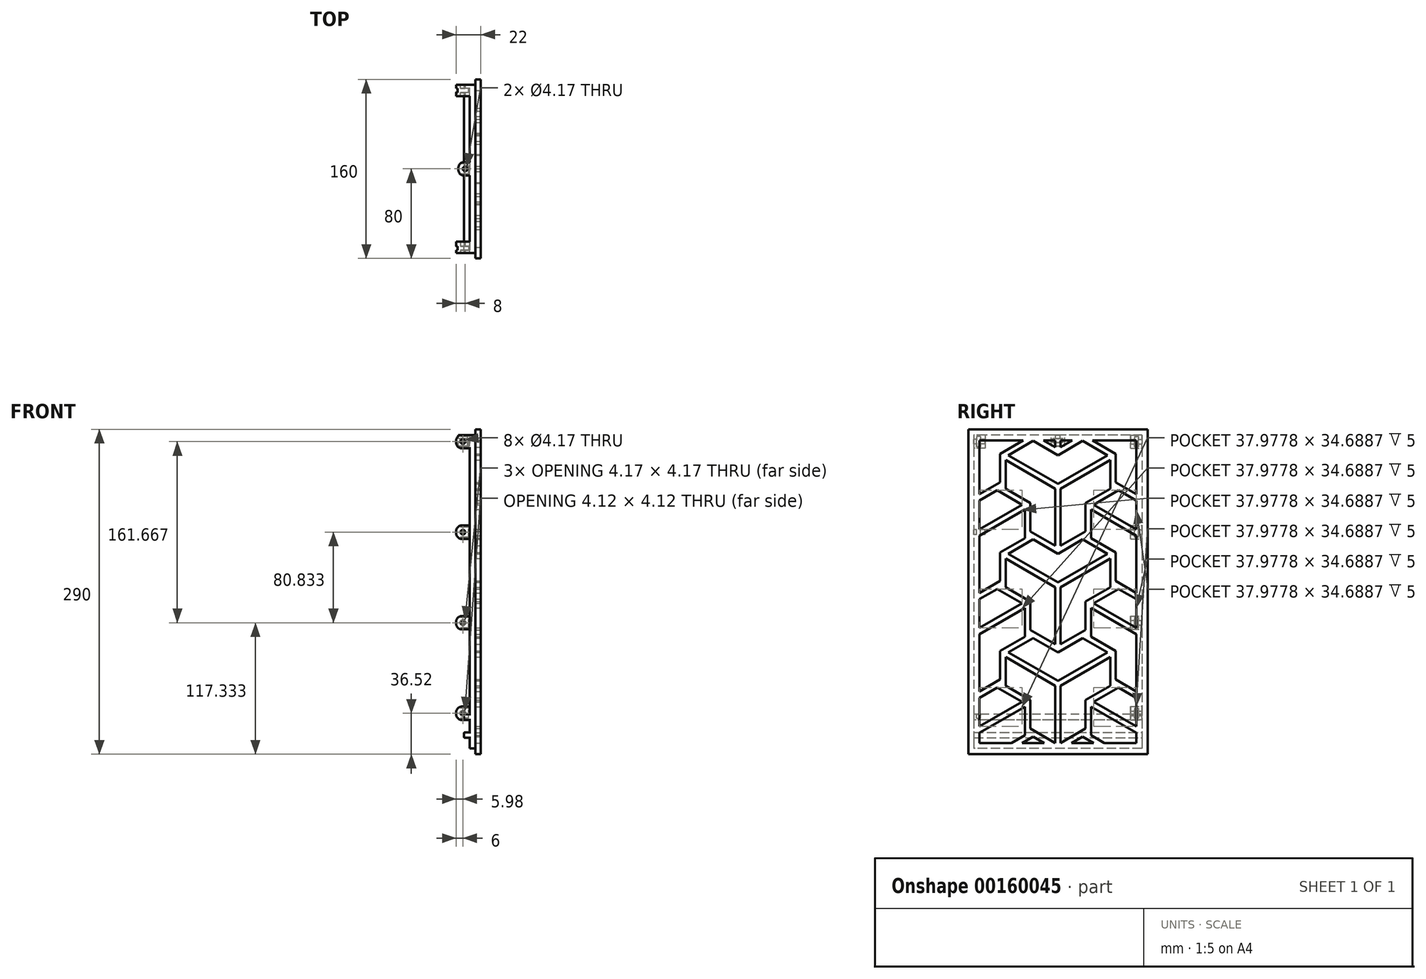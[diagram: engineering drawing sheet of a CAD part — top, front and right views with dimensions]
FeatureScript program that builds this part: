
annotation { "Feature Type Name" : "Feature", "Feature Type Description" : "" }
export const myFeature = defineFeature(function(context is Context, id is Id, definition is map)
    precondition{}
    {
        {
            var Q0;
            Q0=qCreatedBy(makeId("Top.planeOp"),FACE);
            var sketch = newSketch(context, id + "F0", { "sketchPlane" : qUnion([Q0])});
            skLineSegment(sketch, "E0.bottom", {"start": v(-72.5, -75) * mm, "end": v(72.5, -75) * mm});
            skLineSegment(sketch, "E0.top", {"start": v(-72.5, 75) * mm, "end": v(72.5, 75) * mm});
            skLineSegment(sketch, "E0.left", {"start": v(-72.5, -75) * mm, "end": v(-72.5, 75) * mm});
            skLineSegment(sketch, "E0.right", {"start": v(72.5, -75) * mm, "end": v(72.5, 75) * mm});
            skPoint(sketch, "E0.middle", {"position": v(0, 0) * mm});
            skLineSegment(sketch, "E1.bottom", {"start": v(-82.5, -85) * mm, "end": v(82.5, -85) * mm});
            skLineSegment(sketch, "E1.top", {"start": v(-82.5, 85) * mm, "end": v(82.5, 85) * mm});
            skLineSegment(sketch, "E1.left", {"start": v(-82.5, -85) * mm, "end": v(-82.5, 85) * mm});
            skLineSegment(sketch, "E1.right", {"start": v(82.5, -85) * mm, "end": v(82.5, 85) * mm});
            skLineSegment(sketch, "E2", {"start": v(82.5, -80) * mm, "end": v(77.5, -80) * mm});
            skLineSegment(sketch, "E3", {"start": v(77.5, -80) * mm, "end": v(77.5, -75) * mm});
            skLineSegment(sketch, "E4", {"start": v(77.5, -75) * mm, "end": v(72.5, -75) * mm});
            skLineSegment(sketch, "E5", {"start": v(0, -85) * mm, "end": v(0, 85) * mm, "construction": true});
            skLineSegment(sketch, "E6", {"start": v(-82.5, 0) * mm, "end": v(82.5, 0) * mm, "construction": true});
            skLineSegment(sketch, "E7.MirrorCS", {"start": v(-77.5, -75) * mm, "end": v(-72.5, -75) * mm});
            skLineSegment(sketch, "E8.MirrorCS", {"start": v(-77.5, -80) * mm, "end": v(-77.5, -75) * mm});
            skLineSegment(sketch, "E9.MirrorCS", {"start": v(-82.5, -80) * mm, "end": v(-77.5, -80) * mm});
            skLineSegment(sketch, "E10.MirrorCS", {"start": v(82.5, 80) * mm, "end": v(77.5, 80) * mm});
            skLineSegment(sketch, "E11.MirrorCS", {"start": v(77.5, 80) * mm, "end": v(77.5, 75) * mm});
            skLineSegment(sketch, "E12.MirrorCS", {"start": v(77.5, 75) * mm, "end": v(72.5, 75) * mm});
            skLineSegment(sketch, "E13.MirrorCS", {"start": v(-77.5, 75) * mm, "end": v(-72.5, 75) * mm});
            skLineSegment(sketch, "E14.MirrorCS", {"start": v(-77.5, 80) * mm, "end": v(-77.5, 75) * mm});
            skLineSegment(sketch, "E15.MirrorCS", {"start": v(-82.5, 80) * mm, "end": v(-77.5, 80) * mm});
            skSolve(sketch);
        }
        {
            var Q0;
            Q0=makeQuery(id+"F0.imprint","IMPRINT",FACE,{"disambiguationData":[TD([[makeQuery(id+"F0.imprint","IMPRINT",EDGE,{"derivedFrom":sQuery(id+"F0.wireOp",EDGE,"E0.right")}),-1.0]])]});
            extrude(context, id + "F1", {"entities" : qUnion([Q0]), "depth" : 290 * mm});
        }
        {
            var Q0;
            Q0=makeQuery(id+"F1.opExtrude","SWEPT_FACE",FACE,{"disambiguationData":[OSD([sQuery(id+"F0.wireOp",EDGE,"E4")])]});
            var sketch = newSketch(context, id + "F2", { "sketchPlane" : qUnion([Q0])});
            skLineSegment(sketch, "E16.bottom", {"start": v(77.5, 290) * mm, "end": v(72.5, 290) * mm});
            skLineSegment(sketch, "E16.top", {"start": v(77.5, 285) * mm, "end": v(72.5, 285) * mm});
            skLineSegment(sketch, "E16.left", {"start": v(77.5, 290) * mm, "end": v(77.5, 285) * mm});
            skLineSegment(sketch, "E16.right", {"start": v(72.5, 290) * mm, "end": v(72.5, 285) * mm});
            skLineSegment(sketch, "E17.bottom", {"start": v(77.5, 0) * mm, "end": v(72.5, 0) * mm});
            skLineSegment(sketch, "E17.top", {"start": v(77.5, 5) * mm, "end": v(72.5, 5) * mm});
            skLineSegment(sketch, "E17.left", {"start": v(77.5, 0) * mm, "end": v(77.5, 5) * mm});
            skLineSegment(sketch, "E17.right", {"start": v(72.5, 0) * mm, "end": v(72.5, 5) * mm});
            skSolve(sketch);
        }
        {
            var Q0;
            Q0 = qSketchRegion(id + "F2", true);
            extrude(context, id + "F3", {"entities" : qUnion([Q0]), "operationType" : NewBodyOperationType.REMOVE, "endBound" : BoundingType.THROUGH_ALL, "oppositeDirection" : true, "depth" : 25 * mm});
        }
        {
            var Q0;
            Q0=makeQuery(id+"F1.opExtrude","SWEPT_FACE",FACE,{"disambiguationData":[OSD([sQuery(id+"F0.wireOp",EDGE,"E0.right")])]});
            var sketch = newSketch(context, id + "F4", { "sketchPlane" : qUnion([Q0])});
            skLineSegment(sketch, "E18.bottom", {"start": v(-75, 35.5) * mm, "end": v(75, 35.5) * mm});
            skLineSegment(sketch, "E18.top", {"start": v(-75, 30.5) * mm, "end": v(75, 30.5) * mm});
            skLineSegment(sketch, "E18.left", {"start": v(-75, 35.5) * mm, "end": v(-75, 30.5) * mm});
            skLineSegment(sketch, "E18.right", {"start": v(75, 35.5) * mm, "end": v(75, 30.5) * mm});
            skLineSegment(sketch, "E19.bottom", {"start": v(75, 19.5) * mm, "end": v(-75, 19.5) * mm});
            skLineSegment(sketch, "E19.top", {"start": v(75, 14.5) * mm, "end": v(-75, 14.5) * mm});
            skLineSegment(sketch, "E19.left", {"start": v(75, 19.5) * mm, "end": v(75, 14.5) * mm});
            skLineSegment(sketch, "E19.right", {"start": v(-75, 19.5) * mm, "end": v(-75, 14.5) * mm});
            skSolve(sketch);
        }
        {
            var Q0;
            Q0=makeQuery(id+"F4.imprint","IMPRINT",FACE,{"disambiguationData":[TD([[makeQuery(id+"F4.imprint","IMPRINT",EDGE,{"derivedFrom":sQuery(id+"F4.wireOp",EDGE,"jm3xENIU-WNiL-2Yo7-S2n1-P718Q5YoGy5W.bottom")}),-1.0]])]});
            var Q1;
            Q1=makeQuery(id+"F4.imprint","IMPRINT",FACE,{"disambiguationData":[TD([[makeQuery(id+"F4.imprint","IMPRINT",EDGE,{"derivedFrom":sQuery(id+"F4.wireOp",EDGE,"tnRABQw2-jlkN-R6kw-IWLg-kbEZeZclKpCx.bottom")}),1.0]])]});
            var Q2;
            Q2=makeQuery(id+"F4.imprint","IMPRINT",FACE,{"disambiguationData":[TD([[makeQuery(id+"F4.imprint","IMPRINT",EDGE,{"derivedFrom":sQuery(id+"F4.wireOp",EDGE,"E18.bottom")}),-1.0]])]});
            var Q3;
            Q3=makeQuery(id+"F4.imprint","IMPRINT",FACE,{"disambiguationData":[TD([[makeQuery(id+"F4.imprint","IMPRINT",EDGE,{"derivedFrom":sQuery(id+"F4.wireOp",EDGE,"E19.bottom")}),1.0]])]});
            extrude(context, id + "F5", {"entities" : qUnion([Q0, Q1, Q2, Q3]), "operationType" : NewBodyOperationType.ADD, "depth" : 5 * mm});
        }
        {
            var Q0;
            Q0=makeQuery(id+"F1.opExtrude","SWEPT_FACE",FACE,{"disambiguationData":[OSD([sQuery(id+"F0.wireOp",EDGE,"E1.right")])]});
            var sketch = newSketch(context, id + "F6", { "sketchPlane" : qUnion([Q0])});
            skLineSegment(sketch, "E20.left", {"start": v(70, 10) * mm, "end": v(70, 280) * mm, "construction": true});
            skPoint(sketch, "E20.middle", {"position": v(0, 145) * mm});
            skPoint(sketch, "E20.middle.positionSnap0", {"position": v(-80, 145) * mm});
            skPoint(sketch, "E20.middle.positionSnap1", {"position": v(0, 290) * mm});
            skPoint(sketch, "E20.centerSnap0", {"position": v(-80, 145) * mm});
            skPoint(sketch, "E20.centerSnap1", {"position": v(0, 290) * mm});
            skLineSegment(sketch, "E21", {"start": v(-70, 280) * mm, "end": v(70, 280) * mm, "construction": true});
            skLineSegment(sketch, "E22", {"start": v(-70, 10) * mm, "end": v(70, 10) * mm, "construction": true});
            skLineSegment(sketch, "E23", {"start": v(-70, 280) * mm, "end": v(-70, 10) * mm, "construction": true});
            skLineSegment(sketch, "E24", {"start": v(2.5, 10) * mm, "end": v(2.5, 61.05) * mm});
            skLineSegment(sketch, "E25", {"start": v(2.5, 61.05) * mm, "end": v(46.7, 86.57) * mm});
            skLineSegment(sketch, "E26", {"start": v(46.7, 86.57) * mm, "end": v(46.7, 61.05) * mm});
            skLineSegment(sketch, "E27", {"start": v(2.5, 10) * mm, "end": v(24.6, 22.76) * mm});
            skLineSegment(sketch, "E28", {"start": v(24.6, 22.76) * mm, "end": v(24.6, 48.29) * mm});
            skLineSegment(sketch, "E29", {"start": v(24.6, 48.29) * mm, "end": v(46.7, 61.05) * mm});
            skLineSegment(sketch, "E30.1.0", {"start": v(0, 65.38) * mm, "end": v(-44.2, 90.9) * mm});
            skLineSegment(sketch, "E30.1.1", {"start": v(-44.2, 90.9) * mm, "end": v(-22.1, 103.67) * mm});
            skLineSegment(sketch, "E30.1.2", {"start": v(0, 90.9) * mm, "end": v(-22.1, 103.67) * mm});
            skLineSegment(sketch, "E30.1.3", {"start": v(22.1, 103.67) * mm, "end": v(0, 90.9) * mm});
            skLineSegment(sketch, "E30.1.4", {"start": v(44.2, 90.9) * mm, "end": v(22.1, 103.67) * mm});
            skLineSegment(sketch, "E30.1.5", {"start": v(44.2, 90.9) * mm, "end": v(0, 65.38) * mm});
            skLineSegment(sketch, "E30.2.0", {"start": v(-2.5, 61.05) * mm, "end": v(-2.5, 10) * mm});
            skLineSegment(sketch, "E30.2.1", {"start": v(-2.5, 10) * mm, "end": v(-24.6, 22.76) * mm});
            skLineSegment(sketch, "E30.2.2", {"start": v(-24.6, 48.29) * mm, "end": v(-24.6, 22.76) * mm});
            skLineSegment(sketch, "E30.2.3", {"start": v(-46.7, 61.05) * mm, "end": v(-24.6, 48.29) * mm});
            skLineSegment(sketch, "E30.2.4", {"start": v(-46.7, 86.57) * mm, "end": v(-46.7, 61.05) * mm});
            skLineSegment(sketch, "E30.2.5", {"start": v(-46.7, 86.57) * mm, "end": v(-2.5, 61.05) * mm});
            skPoint(sketch, "E30.center", {"position": v(0, 62.5) * mm});
            skLineSegment(sketch, "E31.0.1.0", {"start": v(2.5, 98) * mm, "end": v(2.5, 149.05) * mm});
            skLineSegment(sketch, "E31.0.1.1", {"start": v(2.5, 98) * mm, "end": v(24.6, 110.76) * mm});
            skLineSegment(sketch, "E31.0.1.2", {"start": v(24.6, 110.76) * mm, "end": v(24.6, 136.29) * mm});
            skLineSegment(sketch, "E31.0.1.3", {"start": v(24.6, 136.29) * mm, "end": v(46.7, 149.05) * mm});
            skLineSegment(sketch, "E31.0.1.4", {"start": v(46.7, 174.57) * mm, "end": v(46.7, 149.05) * mm});
            skLineSegment(sketch, "E31.0.1.5", {"start": v(2.5, 149.05) * mm, "end": v(46.7, 174.57) * mm});
            skLineSegment(sketch, "E31.0.1.6", {"start": v(44.2, 178.9) * mm, "end": v(0, 153.38) * mm});
            skLineSegment(sketch, "E31.0.1.7", {"start": v(44.2, 178.9) * mm, "end": v(22.1, 191.67) * mm});
            skLineSegment(sketch, "E31.0.1.8", {"start": v(22.1, 191.67) * mm, "end": v(0, 178.9) * mm});
            skLineSegment(sketch, "E31.0.2.0", {"start": v(2.5, 186) * mm, "end": v(2.5, 237.05) * mm});
            skLineSegment(sketch, "E31.0.2.1", {"start": v(2.5, 186) * mm, "end": v(24.6, 198.76) * mm});
            skLineSegment(sketch, "E31.0.2.2", {"start": v(24.6, 198.76) * mm, "end": v(24.6, 224.29) * mm});
            skLineSegment(sketch, "E31.0.2.3", {"start": v(24.6, 224.29) * mm, "end": v(46.7, 237.05) * mm});
            skLineSegment(sketch, "E31.0.2.4", {"start": v(46.7, 262.57) * mm, "end": v(46.7, 237.05) * mm});
            skLineSegment(sketch, "E31.0.2.5", {"start": v(2.5, 237.05) * mm, "end": v(46.7, 262.57) * mm});
            skLineSegment(sketch, "E31.0.2.6", {"start": v(44.2, 266.9) * mm, "end": v(0, 241.38) * mm});
            skLineSegment(sketch, "E31.0.2.7", {"start": v(44.2, 266.9) * mm, "end": v(22.1, 279.67) * mm});
            skLineSegment(sketch, "E31.0.2.8", {"start": v(22.1, 279.67) * mm, "end": v(0, 266.9) * mm});
            skLineSegment(sketch, "E31.0.3.0", {"start": v(2.5, 274) * mm, "end": v(2.5, 280) * mm});
            skLineSegment(sketch, "E31.0.3.1", {"start": v(2.5, 274) * mm, "end": v(12.9, 280) * mm});
            skLineSegment(sketch, "E32.0.1.5", {"start": v(29.52, 42.41) * mm, "end": v(70, 19.04) * mm});
            skLineSegment(sketch, "E32.0.1.6", {"start": v(29.52, 16.89) * mm, "end": v(41.45, 10) * mm});
            skLineSegment(sketch, "E32.0.1.9", {"start": v(29.52, 42.41) * mm, "end": v(29.52, 16.89) * mm});
            skLineSegment(sketch, "E32.0.1.15", {"start": v(70, 50.34) * mm, "end": v(54.13, 59.5) * mm});
            skLineSegment(sketch, "E32.0.1.16", {"start": v(32.02, 46.74) * mm, "end": v(54.13, 59.5) * mm});
            skLineSegment(sketch, "E32.0.1.17", {"start": v(70, 24.81) * mm, "end": v(32.02, 46.74) * mm});
            skLineSegment(sketch, "E33.0.1.4", {"start": v(70, 112.81) * mm, "end": v(32.02, 134.74) * mm});
            skLineSegment(sketch, "E33.0.1.5", {"start": v(29.52, 130.41) * mm, "end": v(70, 107.04) * mm});
            skLineSegment(sketch, "E33.0.1.7", {"start": v(29.52, 130.41) * mm, "end": v(29.52, 104.89) * mm});
            skLineSegment(sketch, "E33.0.1.9", {"start": v(51.63, 92.12) * mm, "end": v(51.63, 66.6) * mm});
            skLineSegment(sketch, "E33.0.1.10", {"start": v(70, 56) * mm, "end": v(51.63, 66.6) * mm});
            skLineSegment(sketch, "E33.0.1.12", {"start": v(29.52, 104.89) * mm, "end": v(51.63, 92.12) * mm});
            skLineSegment(sketch, "E33.0.1.13", {"start": v(32.02, 134.74) * mm, "end": v(54.13, 147.5) * mm});
            skLineSegment(sketch, "E33.0.1.14", {"start": v(70, 138.34) * mm, "end": v(54.13, 147.5) * mm});
            skLineSegment(sketch, "E33.0.2.4", {"start": v(70, 200.81) * mm, "end": v(32.02, 222.74) * mm});
            skLineSegment(sketch, "E33.0.2.5", {"start": v(29.52, 218.41) * mm, "end": v(70, 195.04) * mm});
            skLineSegment(sketch, "E33.0.2.7", {"start": v(29.52, 218.41) * mm, "end": v(29.52, 192.89) * mm});
            skLineSegment(sketch, "E33.0.2.9", {"start": v(51.63, 180.12) * mm, "end": v(51.63, 154.6) * mm});
            skLineSegment(sketch, "E33.0.2.10", {"start": v(70, 144) * mm, "end": v(51.63, 154.6) * mm});
            skLineSegment(sketch, "E33.0.2.12", {"start": v(29.52, 192.89) * mm, "end": v(51.63, 180.12) * mm});
            skLineSegment(sketch, "E33.0.2.13", {"start": v(32.02, 222.74) * mm, "end": v(54.13, 235.5) * mm});
            skLineSegment(sketch, "E33.0.2.14", {"start": v(70, 226.34) * mm, "end": v(54.13, 235.5) * mm});
            skLineSegment(sketch, "E33.0.3.9", {"start": v(51.63, 268.12) * mm, "end": v(51.63, 242.6) * mm});
            skLineSegment(sketch, "E33.0.3.10", {"start": v(70, 232) * mm, "end": v(51.63, 242.6) * mm});
            skLineSegment(sketch, "E33.0.3.12", {"start": v(31.06, 280) * mm, "end": v(51.63, 268.12) * mm});
            skLineSegment(sketch, "E34", {"start": v(0, 280) * mm, "end": v(0, 10) * mm, "construction": true});
            skLineSegment(sketch, "E35", {"start": v(41.45, 10) * mm, "end": v(70, 10) * mm});
            skLineSegment(sketch, "E36", {"start": v(70, 10) * mm, "end": v(70, 19.04) * mm});
            skLineSegment(sketch, "E37", {"start": v(70, 24.81) * mm, "end": v(70, 50.34) * mm});
            skLineSegment(sketch, "E38", {"start": v(70, 56) * mm, "end": v(70, 107.04) * mm});
            skLineSegment(sketch, "E39", {"start": v(70, 112.81) * mm, "end": v(70, 138.34) * mm});
            skLineSegment(sketch, "E40", {"start": v(70, 144) * mm, "end": v(70, 195.04) * mm});
            skLineSegment(sketch, "E41", {"start": v(70, 200.81) * mm, "end": v(70, 226.34) * mm});
            skLineSegment(sketch, "E42", {"start": v(70, 232) * mm, "end": v(70, 280) * mm});
            skLineSegment(sketch, "E43", {"start": v(12.9, 280) * mm, "end": v(2.5, 280) * mm});
            skLineSegment(sketch, "E44", {"start": v(70, 280) * mm, "end": v(31.06, 280) * mm});
            skLineSegment(sketch, "E45.MirrorCS", {"start": v(-2.5, 274) * mm, "end": v(-12.9, 280) * mm});
            skLineSegment(sketch, "E46.MirrorCS", {"start": v(-2.5, 274) * mm, "end": v(-2.5, 280) * mm});
            skLineSegment(sketch, "E47.MirrorCS", {"start": v(-22.1, 279.67) * mm, "end": v(0, 266.9) * mm});
            skLineSegment(sketch, "E48.MirrorCS", {"start": v(-44.2, 266.9) * mm, "end": v(0, 241.38) * mm});
            skLineSegment(sketch, "E49.MirrorCS", {"start": v(-44.2, 266.9) * mm, "end": v(-22.1, 279.67) * mm});
            skLineSegment(sketch, "E50.MirrorCS", {"start": v(-31.06, 280) * mm, "end": v(-51.63, 268.12) * mm});
            skLineSegment(sketch, "E51.MirrorCS", {"start": v(-51.63, 268.12) * mm, "end": v(-51.63, 242.6) * mm});
            skLineSegment(sketch, "E52.MirrorCS", {"start": v(-70, 232) * mm, "end": v(-51.63, 242.6) * mm});
            skLineSegment(sketch, "E53.MirrorCS", {"start": v(-32.02, 222.74) * mm, "end": v(-54.13, 235.5) * mm});
            skLineSegment(sketch, "E54.MirrorCS", {"start": v(-24.6, 224.29) * mm, "end": v(-46.7, 237.05) * mm});
            skLineSegment(sketch, "E55.MirrorCS", {"start": v(-46.7, 262.57) * mm, "end": v(-46.7, 237.05) * mm});
            skLineSegment(sketch, "E56.MirrorCS", {"start": v(-2.5, 237.05) * mm, "end": v(-46.7, 262.57) * mm});
            skLineSegment(sketch, "E57.MirrorCS", {"start": v(-2.5, 186) * mm, "end": v(-2.5, 237.05) * mm});
            skLineSegment(sketch, "E58.MirrorCS", {"start": v(-2.5, 186) * mm, "end": v(-24.6, 198.76) * mm});
            skLineSegment(sketch, "E59.MirrorCS", {"start": v(-24.6, 198.76) * mm, "end": v(-24.6, 224.29) * mm});
            skLineSegment(sketch, "E60.MirrorCS", {"start": v(-29.52, 218.41) * mm, "end": v(-29.52, 192.89) * mm});
            skLineSegment(sketch, "E61.MirrorCS", {"start": v(-29.52, 218.41) * mm, "end": v(-70, 195.04) * mm});
            skLineSegment(sketch, "E62.MirrorCS", {"start": v(-70, 200.81) * mm, "end": v(-32.02, 222.74) * mm});
            skLineSegment(sketch, "E63.MirrorCS", {"start": v(-70, 226.34) * mm, "end": v(-54.13, 235.5) * mm});
            skLineSegment(sketch, "E64.MirrorCS", {"start": v(-44.2, 178.9) * mm, "end": v(0, 153.38) * mm});
            skLineSegment(sketch, "E65.MirrorCS", {"start": v(-44.2, 178.9) * mm, "end": v(-22.1, 191.67) * mm});
            skLineSegment(sketch, "E66.MirrorCS", {"start": v(-22.1, 191.67) * mm, "end": v(0, 178.9) * mm});
            skLineSegment(sketch, "E67.MirrorCS", {"start": v(-29.52, 192.89) * mm, "end": v(-51.63, 180.12) * mm});
            skLineSegment(sketch, "E68.MirrorCS", {"start": v(-51.63, 180.12) * mm, "end": v(-51.63, 154.6) * mm});
            skLineSegment(sketch, "E69.MirrorCS", {"start": v(-70, 144) * mm, "end": v(-51.63, 154.6) * mm});
            skLineSegment(sketch, "E70.MirrorCS", {"start": v(-2.5, 149.05) * mm, "end": v(-46.7, 174.57) * mm});
            skLineSegment(sketch, "E71.MirrorCS", {"start": v(-46.7, 174.57) * mm, "end": v(-46.7, 149.05) * mm});
            skLineSegment(sketch, "E72.MirrorCS", {"start": v(-24.6, 136.29) * mm, "end": v(-46.7, 149.05) * mm});
            skLineSegment(sketch, "E73.MirrorCS", {"start": v(-24.6, 110.76) * mm, "end": v(-24.6, 136.29) * mm});
            skLineSegment(sketch, "E74.MirrorCS", {"start": v(-2.5, 98) * mm, "end": v(-24.6, 110.76) * mm});
            skLineSegment(sketch, "E75.MirrorCS", {"start": v(-2.5, 98) * mm, "end": v(-2.5, 149.05) * mm});
            skLineSegment(sketch, "E76.MirrorCS", {"start": v(-29.52, 16.89) * mm, "end": v(-41.45, 10) * mm});
            skLineSegment(sketch, "E77.MirrorCS", {"start": v(-29.52, 42.41) * mm, "end": v(-29.52, 16.89) * mm});
            skLineSegment(sketch, "E78.MirrorCS", {"start": v(-29.52, 42.41) * mm, "end": v(-70, 19.04) * mm});
            skLineSegment(sketch, "E79.MirrorCS", {"start": v(-70, 24.81) * mm, "end": v(-32.02, 46.74) * mm});
            skLineSegment(sketch, "E80.MirrorCS", {"start": v(-32.02, 46.74) * mm, "end": v(-54.13, 59.5) * mm});
            skLineSegment(sketch, "E81.MirrorCS", {"start": v(-70, 50.34) * mm, "end": v(-54.13, 59.5) * mm});
            skLineSegment(sketch, "E82.MirrorCS", {"start": v(-70, 56) * mm, "end": v(-51.63, 66.6) * mm});
            skLineSegment(sketch, "E83.MirrorCS", {"start": v(-51.63, 92.12) * mm, "end": v(-51.63, 66.6) * mm});
            skLineSegment(sketch, "E84.MirrorCS", {"start": v(-29.52, 104.89) * mm, "end": v(-51.63, 92.12) * mm});
            skLineSegment(sketch, "E85.MirrorCS", {"start": v(-29.52, 130.41) * mm, "end": v(-29.52, 104.89) * mm});
            skLineSegment(sketch, "E86.MirrorCS", {"start": v(-29.52, 130.41) * mm, "end": v(-70, 107.04) * mm});
            skLineSegment(sketch, "E87.MirrorCS", {"start": v(-70, 112.81) * mm, "end": v(-32.02, 134.74) * mm});
            skLineSegment(sketch, "E88.MirrorCS", {"start": v(-32.02, 134.74) * mm, "end": v(-54.13, 147.5) * mm});
            skLineSegment(sketch, "E89.MirrorCS", {"start": v(-70, 138.34) * mm, "end": v(-54.13, 147.5) * mm});
            skLineSegment(sketch, "E90", {"start": v(-41.45, 10) * mm, "end": v(-70, 10) * mm});
            skLineSegment(sketch, "E91", {"start": v(-70, 10) * mm, "end": v(-70, 19.04) * mm});
            skLineSegment(sketch, "E92", {"start": v(-70, 24.81) * mm, "end": v(-70, 50.34) * mm});
            skLineSegment(sketch, "E93", {"start": v(-70, 56) * mm, "end": v(-70, 107.04) * mm});
            skLineSegment(sketch, "E94", {"start": v(-70, 112.81) * mm, "end": v(-70, 138.34) * mm});
            skLineSegment(sketch, "E95", {"start": v(-70, 195.04) * mm, "end": v(-70, 144) * mm});
            skLineSegment(sketch, "E96", {"start": v(-70, 200.81) * mm, "end": v(-70, 226.34) * mm});
            skLineSegment(sketch, "E97", {"start": v(-70, 232) * mm, "end": v(-70, 280) * mm});
            skLineSegment(sketch, "E98", {"start": v(-70, 280) * mm, "end": v(-31.06, 280) * mm});
            skLineSegment(sketch, "E99", {"start": v(-2.5, 280) * mm, "end": v(-12.9, 280) * mm});
            skLineSegment(sketch, "E100.0.1.0", {"start": v(22.1, 15.67) * mm, "end": v(12.3, 10) * mm});
            skLineSegment(sketch, "E100.0.1.1", {"start": v(31.92, 10) * mm, "end": v(22.1, 15.67) * mm});
            skLineSegment(sketch, "E100.0.1.2", {"start": v(-12.3, 10) * mm, "end": v(-22.1, 15.67) * mm});
            skLineSegment(sketch, "E100.0.1.3", {"start": v(-31.92, 10) * mm, "end": v(-22.1, 15.67) * mm});
            skLineSegment(sketch, "E100.direction1", {"start": v(0, 90.9) * mm, "end": v(25, 90.9) * mm, "construction": true});
            skLineSegment(sketch, "E101", {"start": v(-31.92, 10) * mm, "end": v(-12.3, 10) * mm});
            skLineSegment(sketch, "E102", {"start": v(12.3, 10) * mm, "end": v(31.92, 10) * mm});
            skSolve(sketch);
        }
        {
            var Q0;
            Q0 = qSketchRegion(id + "F6", true);
            extrude(context, id + "F7", {"entities" : qUnion([Q0]), "operationType" : NewBodyOperationType.REMOVE, "oppositeDirection" : true, "depth" : 5 * mm});
        }
        {
            var Q0;
            Q0=makeQuery(id+"F5.boolean.opBoolean","MERGE",FACE,{"derivedFrom":[makeQuery(id+"F1.opExtrude","SWEPT_FACE",FACE,{"disambiguationData":[OSD([sQuery(id+"F0.wireOp",EDGE,"E4")])]}),makeQuery(id+"F5.opExtrude","SWEPT_FACE",FACE,{"disambiguationData":[OSD([sQuery(id+"F4.wireOp",EDGE,"E18.right")])]}),makeQuery(id+"F5.opExtrude","SWEPT_FACE",FACE,{"disambiguationData":[OSD([sQuery(id+"F4.wireOp",EDGE,"E19.left")])]})]});
            var sketch = newSketch(context, id + "F8", { "sketchPlane" : qUnion([Q0])});
            skPoint(sketch, "E103.visualSharp", {"position": v(-70.5, -71.14) * mm});
            skLineSegment(sketch, "E104.MirrorCS", {"start": v(60.5, 280) * mm, "end": v(60.5, 278) * mm});
            skArc(sketch, "E105.MirrorCS", {"start": v(60.5, 280) * mm, "mid": v(61.96, 283.54) * mm, "end": v(65.5, 285) * mm});
            skArc(sketch, "E106.MirrorCS", {"start": v(65.5, 273) * mm, "mid": v(61.96, 274.46) * mm, "end": v(60.5, 278) * mm});
            skCircle(sketch, "E107.MirrorC", {"center": v(66.5, 198.17) * mm, "radius": 2.08 * mm});
            skArc(sketch, "E108.MirrorCS", {"start": v(65.5, 192.17) * mm, "mid": v(61.96, 193.63) * mm, "end": v(60.5, 197.17) * mm});
            skArc(sketch, "E109.MirrorCS", {"start": v(60.5, 37.5) * mm, "mid": v(61.96, 41.04) * mm, "end": v(65.5, 42.5) * mm});
            skLineSegment(sketch, "E110.MirrorCS", {"start": v(60.5, 35.5) * mm, "end": v(60.5, 37.5) * mm});
            skLineSegment(sketch, "E111.MirrorCS", {"start": v(60.5, 199.17) * mm, "end": v(60.5, 197.17) * mm});
            skLineSegment(sketch, "E112.MirrorCS", {"start": v(72.5, 192.17) * mm, "end": v(65.5, 192.17) * mm});
            skLineSegment(sketch, "E113.MirrorCS", {"start": v(72.5, 204.17) * mm, "end": v(72.5, 192.17) * mm});
            skLineSegment(sketch, "E114.MirrorCS", {"start": v(72.5, 204.17) * mm, "end": v(65.5, 204.17) * mm});
            skArc(sketch, "E115.MirrorCS", {"start": v(60.5, 118.33) * mm, "mid": v(61.96, 121.87) * mm, "end": v(65.5, 123.33) * mm});
            skLineSegment(sketch, "E116.MirrorCS", {"start": v(72.5, 198.17) * mm, "end": v(60.5, 198.17) * mm, "construction": true});
            skArc(sketch, "E117.MirrorCS", {"start": v(60.5, 199.17) * mm, "mid": v(61.96, 202.7) * mm, "end": v(65.5, 204.17) * mm});
            skArc(sketch, "E118.MirrorCS", {"start": v(65.5, 30.5) * mm, "mid": v(61.96, 31.96) * mm, "end": v(60.5, 35.5) * mm});
            skLineSegment(sketch, "E119.MirrorCS", {"start": v(60.5, 118.33) * mm, "end": v(60.5, 116.33) * mm});
            skArc(sketch, "E120.MirrorCS", {"start": v(65.5, 111.33) * mm, "mid": v(61.96, 112.8) * mm, "end": v(60.5, 116.33) * mm});
            skLineSegment(sketch, "E121.MirrorCS", {"start": v(72.5, 285) * mm, "end": v(72.5, 273) * mm});
            skLineSegment(sketch, "E122.MirrorCS", {"start": v(72.5, 279) * mm, "end": v(60.5, 279) * mm, "construction": true});
            skLineSegment(sketch, "E123.MirrorCS", {"start": v(72.5, 123.33) * mm, "end": v(72.5, 111.33) * mm});
            skCircle(sketch, "E124.MirrorC", {"center": v(66.5, 117.33) * mm, "radius": 2.08 * mm});
            skCircle(sketch, "E125.MirrorC", {"center": v(66.5, 36.5) * mm, "radius": 2.08 * mm});
            skLineSegment(sketch, "E126.MirrorCS", {"start": v(65.5, 42.5) * mm, "end": v(72.5, 42.5) * mm});
            skLineSegment(sketch, "E127.MirrorCS", {"start": v(72.5, 36.5) * mm, "end": v(60.5, 36.5) * mm, "construction": true});
            skLineSegment(sketch, "E128.MirrorCS", {"start": v(65.5, 30.5) * mm, "end": v(72.5, 30.5) * mm});
            skLineSegment(sketch, "E129.MirrorCS", {"start": v(72.5, 111.33) * mm, "end": v(65.5, 111.33) * mm});
            skLineSegment(sketch, "E130.MirrorCS", {"start": v(72.5, 273) * mm, "end": v(65.5, 273) * mm});
            skCircle(sketch, "E131.MirrorC", {"center": v(66.5, 279) * mm, "radius": 2.08 * mm});
            skLineSegment(sketch, "E132.MirrorCS", {"start": v(72.5, 285) * mm, "end": v(65.5, 285) * mm});
            skLineSegment(sketch, "E133.MirrorCS", {"start": v(72.5, 123.33) * mm, "end": v(65.5, 123.33) * mm});
            skLineSegment(sketch, "E134.MirrorCS", {"start": v(72.5, 30.5) * mm, "end": v(72.5, 42.5) * mm});
            skLineSegment(sketch, "E135.MirrorCS", {"start": v(72.5, 117.33) * mm, "end": v(60.5, 117.33) * mm, "construction": true});
            skPoint(sketch, "E136.MirrorP", {"position": v(60.5, 42.5) * mm});
            skPoint(sketch, "E137.MirrorP", {"position": v(60.5, 192.17) * mm});
            skPoint(sketch, "E138.MirrorP", {"position": v(60.5, 273) * mm});
            skLineSegment(sketch, "E139.MirrorCS", {"start": v(69, 273) * mm, "end": v(69, 204.17) * mm, "construction": true});
            skPoint(sketch, "E140.MirrorP", {"position": v(60.5, -71.14) * mm});
            skPoint(sketch, "E141.MirrorP", {"position": v(60.5, 123.33) * mm});
            skLineSegment(sketch, "E142.MirrorCS", {"start": v(69, 111.33) * mm, "end": v(69, 42.5) * mm, "construction": true});
            skLineSegment(sketch, "E143.MirrorCS", {"start": v(69, 192.17) * mm, "end": v(69, 123.33) * mm, "construction": true});
            skPoint(sketch, "E144.MirrorP", {"position": v(60.5, 285) * mm});
            skPoint(sketch, "E145.MirrorP", {"position": v(60.5, 204.17) * mm});
            skPoint(sketch, "E146.MirrorP", {"position": v(60.5, 111.33) * mm});
            skSolve(sketch);
        }
        {
            var Q0;
            Q0=makeQuery(id+"F8.imprint","IMPRINT",FACE,{"disambiguationData":[TD([[makeQuery(id+"F8.imprint","IMPRINT",EDGE,{"derivedFrom":sQuery(id+"F8.wireOp",EDGE,"E107.MirrorC")}),1.0]])]});
            var Q1;
            Q1=makeQuery(id+"F8.imprint","IMPRINT",FACE,{"disambiguationData":[TD([[makeQuery(id+"F8.imprint","IMPRINT",EDGE,{"derivedFrom":sQuery(id+"F8.wireOp",EDGE,"E115.MirrorCS")}),-1.0]])]});
            var Q2;
            Q2=makeQuery(id+"F8.imprint","IMPRINT",FACE,{"disambiguationData":[TD([[makeQuery(id+"F8.imprint","IMPRINT",EDGE,{"derivedFrom":sQuery(id+"F8.wireOp",EDGE,"E109.MirrorCS")}),-1.0]])]});
            var Q3;
            Q3=makeQuery(id+"F8.imprint","IMPRINT",FACE,{"disambiguationData":[TD([[makeQuery(id+"F8.imprint","IMPRINT",EDGE,{"derivedFrom":sQuery(id+"F8.wireOp",EDGE,"E104.MirrorCS")}),1.0]])]});
            extrude(context, id + "F9", {"entities" : qUnion([Q0, Q1, Q2, Q3]), "operationType" : NewBodyOperationType.ADD, "oppositeDirection" : true, "depth" : 10 * mm});
        }
        {
            var Q0;
            Q0=makeQuery(id+"F5.boolean.opBoolean","MERGE",FACE,{"derivedFrom":[makeQuery(id+"F1.opExtrude","SWEPT_FACE",FACE,{"disambiguationData":[OSD([sQuery(id+"F0.wireOp",EDGE,"E12.MirrorCS")])]}),makeQuery(id+"F5.opExtrude","SWEPT_FACE",FACE,{"disambiguationData":[OSD([sQuery(id+"F4.wireOp",EDGE,"E18.left")])]}),makeQuery(id+"F5.opExtrude","SWEPT_FACE",FACE,{"disambiguationData":[OSD([sQuery(id+"F4.wireOp",EDGE,"E19.right")])]})]});
            var sketch = newSketch(context, id + "F10", { "sketchPlane" : qUnion([Q0])});
            skLineSegment(sketch, "E147.bottom", {"start": v(-72.5, 285) * mm, "end": v(-65.5, 285) * mm});
            skLineSegment(sketch, "E147.top", {"start": v(-72.5, 273) * mm, "end": v(-65.5, 273) * mm});
            skLineSegment(sketch, "E147.left", {"start": v(-72.5, 285) * mm, "end": v(-72.5, 273) * mm});
            skLineSegment(sketch, "E147.right", {"start": v(-60.5, 280) * mm, "end": v(-60.5, 278) * mm});
            skPoint(sketch, "E148.visualSharp", {"position": v(-60.5, 285) * mm});
            skArc(sketch, "E148.filletArc", {"start": v(-60.5, 280) * mm, "mid": v(-61.96, 283.54) * mm, "end": v(-65.5, 285) * mm});
            skPoint(sketch, "E149.visualSharp", {"position": v(-60.5, 273) * mm});
            skArc(sketch, "E149.filletArc", {"start": v(-65.5, 273) * mm, "mid": v(-61.96, 274.46) * mm, "end": v(-60.5, 278) * mm});
            skLineSegment(sketch, "E150.bottom", {"start": v(-65.5, 30.5) * mm, "end": v(-72.5, 30.5) * mm});
            skLineSegment(sketch, "E150.top", {"start": v(-65.5, 42.5) * mm, "end": v(-72.5, 42.5) * mm});
            skLineSegment(sketch, "E150.left", {"start": v(-60.5, 35.5) * mm, "end": v(-60.5, 37.5) * mm});
            skLineSegment(sketch, "E150.right", {"start": v(-72.5, 30.5) * mm, "end": v(-72.5, 42.5) * mm});
            skPoint(sketch, "E151.visualSharp", {"position": v(-60.5, 42.5) * mm});
            skArc(sketch, "E151.filletArc", {"start": v(-60.5, 37.5) * mm, "mid": v(-61.96, 41.04) * mm, "end": v(-65.5, 42.5) * mm});
            skPoint(sketch, "E152.visualSharp", {"position": v(-60.5, 86.6) * mm});
            skArc(sketch, "E152.filletArc", {"start": v(-65.5, 30.5) * mm, "mid": v(-61.96, 31.96) * mm, "end": v(-60.5, 35.5) * mm});
            skLineSegment(sketch, "E153.bottom", {"start": v(-72.5, 204.17) * mm, "end": v(-65.5, 204.17) * mm});
            skLineSegment(sketch, "E153.top", {"start": v(-72.5, 192.17) * mm, "end": v(-65.5, 192.17) * mm});
            skLineSegment(sketch, "E153.left", {"start": v(-72.5, 204.17) * mm, "end": v(-72.5, 192.17) * mm});
            skLineSegment(sketch, "E153.right", {"start": v(-60.5, 199.17) * mm, "end": v(-60.5, 197.17) * mm});
            skLineSegment(sketch, "E154.bottom", {"start": v(-72.5, 123.33) * mm, "end": v(-65.5, 123.33) * mm});
            skLineSegment(sketch, "E154.top", {"start": v(-72.5, 111.33) * mm, "end": v(-65.5, 111.33) * mm});
            skLineSegment(sketch, "E154.left", {"start": v(-72.5, 123.33) * mm, "end": v(-72.5, 111.33) * mm});
            skLineSegment(sketch, "E154.right", {"start": v(-60.5, 118.33) * mm, "end": v(-60.5, 116.33) * mm});
            skPoint(sketch, "E155.visualSharp", {"position": v(-60.5, 204.17) * mm});
            skArc(sketch, "E155.filletArc", {"start": v(-60.5, 199.17) * mm, "mid": v(-61.96, 202.7) * mm, "end": v(-65.5, 204.17) * mm});
            skPoint(sketch, "E156.visualSharp", {"position": v(-60.5, 192.17) * mm});
            skArc(sketch, "E156.filletArc", {"start": v(-65.5, 192.17) * mm, "mid": v(-61.96, 193.63) * mm, "end": v(-60.5, 197.17) * mm});
            skPoint(sketch, "E157.visualSharp", {"position": v(-60.5, 123.33) * mm});
            skArc(sketch, "E157.filletArc", {"start": v(-60.5, 118.33) * mm, "mid": v(-61.96, 121.87) * mm, "end": v(-65.5, 123.33) * mm});
            skPoint(sketch, "E158.visualSharp", {"position": v(-60.5, 111.33) * mm});
            skArc(sketch, "E158.filletArc", {"start": v(-65.5, 111.33) * mm, "mid": v(-61.96, 112.8) * mm, "end": v(-60.5, 116.33) * mm});
            skLineSegment(sketch, "E159", {"start": v(-69, 273) * mm, "end": v(-69, 204.17) * mm, "construction": true});
            skLineSegment(sketch, "E160", {"start": v(-69, 192.17) * mm, "end": v(-69, 123.33) * mm, "construction": true});
            skLineSegment(sketch, "E161", {"start": v(-69, 111.33) * mm, "end": v(-69, 42.5) * mm, "construction": true});
            skLineSegment(sketch, "E162", {"start": v(-72.5, 279) * mm, "end": v(-60.5, 279) * mm, "construction": true});
            skCircle(sketch, "E163", {"center": v(-66.5, 279) * mm, "radius": 2.08 * mm});
            skLineSegment(sketch, "E164", {"start": v(-72.5, 198.17) * mm, "end": v(-60.5, 198.17) * mm, "construction": true});
            skLineSegment(sketch, "E165", {"start": v(-72.5, 117.33) * mm, "end": v(-60.5, 117.33) * mm, "construction": true});
            skLineSegment(sketch, "E166", {"start": v(-72.5, 36.5) * mm, "end": v(-60.5, 36.5) * mm, "construction": true});
            skCircle(sketch, "E167", {"center": v(-66.5, 36.5) * mm, "radius": 2.08 * mm});
            skCircle(sketch, "E168", {"center": v(-66.5, 117.33) * mm, "radius": 2.08 * mm});
            skCircle(sketch, "E169", {"center": v(-66.5, 198.17) * mm, "radius": 2.08 * mm});
            skSolve(sketch);
        }
        {
            var Q0;
            Q0 = qSketchRegion(id + "F10", true);
            extrude(context, id + "F11", {"entities" : qUnion([Q0]), "operationType" : NewBodyOperationType.ADD, "oppositeDirection" : true, "depth" : 10 * mm});
        }
        {
            var Q0;
            Q0=makeQuery(id+"F11.boolean.opBoolean","MERGE",FACE,{"derivedFrom":[makeQuery(id+"F9.boolean.opBoolean","MERGE",FACE,{"derivedFrom":[makeQuery(id+"F3.boolean.opBoolean","COPY",FACE,{"derivedFrom":makeQuery(id+"F3.opExtrude","SWEPT_FACE",FACE,{"disambiguationData":[OSD([sQuery(id+"F2.wireOp",EDGE,"E16.top")])]})}),makeQuery(id+"F9.opExtrude","SWEPT_FACE",FACE,{"disambiguationData":[OSD([sQuery(id+"F8.wireOp",EDGE,"E132.MirrorCS")])]})]}),makeQuery(id+"F11.opExtrude","SWEPT_FACE",FACE,{"disambiguationData":[OSD([sQuery(id+"F10.wireOp",EDGE,"E147.bottom")])]})]});
            var sketch = newSketch(context, id + "F12", { "sketchPlane" : qUnion([Q0])});
            skLineSegment(sketch, "E170.bottom", {"start": v(72.5, -6) * mm, "end": v(67.5, -6) * mm});
            skLineSegment(sketch, "E170.top", {"start": v(72.5, 6) * mm, "end": v(67.5, 6) * mm});
            skLineSegment(sketch, "E170.left", {"start": v(72.5, -6) * mm, "end": v(72.5, 6) * mm});
            skLineSegment(sketch, "E170.right", {"start": v(62.5, -1) * mm, "end": v(62.5, 1) * mm});
            skPoint(sketch, "E170.middle", {"position": v(67.5, 0) * mm});
            skPoint(sketch, "E171.visualSharp", {"position": v(62.5, -6) * mm});
            skArc(sketch, "E171.filletArc", {"start": v(62.5, -1) * mm, "mid": v(63.96, -4.54) * mm, "end": v(67.5, -6) * mm});
            skPoint(sketch, "E172.visualSharp", {"position": v(62.5, 6) * mm});
            skArc(sketch, "E172.filletArc", {"start": v(67.5, 6) * mm, "mid": v(63.96, 4.54) * mm, "end": v(62.5, 1) * mm});
            skCircle(sketch, "E173", {"center": v(68.5, 0) * mm, "radius": 2.08 * mm});
            skPoint(sketch, "E173.centerSnap0", {"position": v(62.5, 0) * mm});
            skSolve(sketch);
        }
        {
            var Q0;
            Q0=makeQuery(id+"F12.imprint","IMPRINT",FACE,{"disambiguationData":[TD([[makeQuery(id+"F12.imprint","IMPRINT",EDGE,{"derivedFrom":sQuery(id+"F12.wireOp",EDGE,"E170.bottom")}),-1.0]])]});
            extrude(context, id + "F13", {"entities" : qUnion([Q0]), "operationType" : NewBodyOperationType.ADD, "oppositeDirection" : true, "depth" : 10 * mm});
        }
        {
            var Q0;
            Q0=makeQuery(id+"F3.boolean.opBoolean","COPY",EDGE,{"derivedFrom":makeQuery(id+"F3.opExtrude","SWEPT_EDGE",EDGE,{"disambiguationData":[OSD([sQuery(id+"F0.wireOp",EDGE,"E0.bottom"),sQuery(id+"F0.wireOp",EDGE,"E0.right"),sQuery(id+"F0.wireOp",EDGE,"E4"),sQuery(id+"F2.wireOp",EDGE,"E16.top"),sQuery(id+"F2.wireOp",EDGE,"E16.right")])]})});
            var Q1;
            Q1=makeQuery(id+"F1.opExtrude","SWEPT_EDGE",EDGE,{"disambiguationData":[OSD([sQuery(id+"F0.wireOp",EDGE,"E0.bottom"),sQuery(id+"F0.wireOp",EDGE,"E0.right"),sQuery(id+"F0.wireOp",EDGE,"E4")])]});
            var Q2;
            Q2=makeQuery(id+"F3.boolean.opBoolean","COPY",EDGE,{"derivedFrom":makeQuery(id+"F3.opExtrude","SWEPT_EDGE",EDGE,{"disambiguationData":[OSD([sQuery(id+"F0.wireOp",EDGE,"E0.bottom"),sQuery(id+"F0.wireOp",EDGE,"E0.right"),sQuery(id+"F0.wireOp",EDGE,"E4"),sQuery(id+"F2.wireOp",EDGE,"E17.top"),sQuery(id+"F2.wireOp",EDGE,"E17.right")])]})});
            var Q3;
            Q3=makeQuery(id+"F1.opExtrude","SWEPT_EDGE",EDGE,{"disambiguationData":[OSD([sQuery(id+"F0.wireOp",EDGE,"E0.top"),sQuery(id+"F0.wireOp",EDGE,"E0.right"),sQuery(id+"F0.wireOp",EDGE,"E12.MirrorCS")])]});
            var Q4;
            Q4=makeQuery(id+"F5.opExtrude","CAP_EDGE",EDGE,{"disambiguationData":[OSD([sQuery(id+"F4.wireOp",EDGE,"E19.top")])],"isStart":false});
            var Q5;
            Q5=makeQuery(id+"F5.opExtrude","CAP_EDGE",EDGE,{"disambiguationData":[OSD([sQuery(id+"F4.wireOp",EDGE,"E18.top")])],"isStart":false});
            var Q6;
            Q6=makeQuery(id+"F5.opExtrude","CAP_EDGE",EDGE,{"disambiguationData":[OSD([sQuery(id+"F4.wireOp",EDGE,"E19.bottom")])],"isStart":false});
            var Q7;
            Q7=makeQuery(id+"F5.opExtrude","CAP_EDGE",EDGE,{"disambiguationData":[OSD([sQuery(id+"F4.wireOp",EDGE,"E18.bottom")])],"isStart":false});
            var Q8;
            Q8=makeQuery(id+"F5.opExtrude","CAP_EDGE",EDGE,{"disambiguationData":[OSD([sQuery(id+"F4.wireOp",EDGE,"tnRABQw2-jlkN-R6kw-IWLg-kbEZeZclKpCx.bottom")])],"isStart":false});
            var Q9;
            Q9=makeQuery(id+"F5.opExtrude","CAP_EDGE",EDGE,{"disambiguationData":[OSD([sQuery(id+"F4.wireOp",EDGE,"jm3xENIU-WNiL-2Yo7-S2n1-P718Q5YoGy5W.bottom")])],"isStart":false});
            var Q10;
            Q10=makeQuery(id+"F5.opExtrude","CAP_EDGE",EDGE,{"disambiguationData":[OSD([sQuery(id+"F4.wireOp",EDGE,"jm3xENIU-WNiL-2Yo7-S2n1-P718Q5YoGy5W.top")])],"isStart":false});
            var Q11;
            Q11=makeQuery(id+"F5.opExtrude","CAP_EDGE",EDGE,{"disambiguationData":[OSD([sQuery(id+"F4.wireOp",EDGE,"tnRABQw2-jlkN-R6kw-IWLg-kbEZeZclKpCx.top")])],"isStart":false});
            fillet(context, id + "F14", {"entities" : qUnion([Q0, Q1, Q2, Q3, Q4, Q5, Q6, Q7, Q8, Q9, Q10, Q11]), "radius" : 1 * mm, "tangentPropagation" : true, "allowEdgeOverflow" : false});
        }
        {
            var Q0;
            Q0=makeQuery(id+"F11.opExtrude","SWEPT_FACE",FACE,{"disambiguationData":[OSD([sQuery(id+"F10.wireOp",EDGE,"E147.right")])]});
            var sketch = newSketch(context, id + "F15", { "sketchPlane" : qUnion([Q0])});
            skLineSegment(sketch, "E174.bottom", {"start": v(-68.25, 274.5) * mm, "end": v(-71.75, 274.5) * mm});
            skLineSegment(sketch, "E174.top", {"start": v(-68.25, 283.5) * mm, "end": v(-71.75, 283.5) * mm});
            skLineSegment(sketch, "E174.left", {"start": v(-68.25, 274.5) * mm, "end": v(-68.25, 283.5) * mm});
            skLineSegment(sketch, "E174.right", {"start": v(-71.75, 274.5) * mm, "end": v(-71.75, 283.5) * mm});
            skPoint(sketch, "E174.middle", {"position": v(-70, 279) * mm});
            skPoint(sketch, "E174.middle.positionSnap0", {"position": v(-70, 280) * mm});
            skPoint(sketch, "E174.middle.positionSnap1", {"position": v(-75, 279) * mm});
            skPoint(sketch, "E174.centerSnap0", {"position": v(-70, 280) * mm});
            skPoint(sketch, "E174.centerSnap1", {"position": v(-75, 279) * mm});
            skLineSegment(sketch, "E175.0.1.0", {"start": v(-68.25, 193.67) * mm, "end": v(-71.75, 193.67) * mm});
            skLineSegment(sketch, "E175.0.1.1", {"start": v(-68.25, 202.67) * mm, "end": v(-71.75, 202.67) * mm});
            skLineSegment(sketch, "E175.0.1.2", {"start": v(-68.25, 193.67) * mm, "end": v(-68.25, 202.67) * mm});
            skLineSegment(sketch, "E175.0.1.3", {"start": v(-71.75, 193.67) * mm, "end": v(-71.75, 202.67) * mm});
            skPoint(sketch, "E175.0.1.4", {"position": v(-70, 199.17) * mm});
            skPoint(sketch, "E175.0.1.5", {"position": v(-75, 198.17) * mm});
            skPoint(sketch, "E175.0.1.6", {"position": v(-70, 198.17) * mm});
            skPoint(sketch, "E175.0.1.7", {"position": v(-70, 199.17) * mm});
            skPoint(sketch, "E175.0.1.8", {"position": v(-75, 198.17) * mm});
            skLineSegment(sketch, "E175.0.2.0", {"start": v(-68.25, 112.83) * mm, "end": v(-71.75, 112.83) * mm});
            skLineSegment(sketch, "E175.0.2.1", {"start": v(-68.25, 121.83) * mm, "end": v(-71.75, 121.83) * mm});
            skLineSegment(sketch, "E175.0.2.2", {"start": v(-68.25, 112.83) * mm, "end": v(-68.25, 121.83) * mm});
            skLineSegment(sketch, "E175.0.2.3", {"start": v(-71.75, 112.83) * mm, "end": v(-71.75, 121.83) * mm});
            skPoint(sketch, "E175.0.2.4", {"position": v(-70, 118.33) * mm});
            skPoint(sketch, "E175.0.2.5", {"position": v(-75, 117.33) * mm});
            skPoint(sketch, "E175.0.2.6", {"position": v(-70, 117.33) * mm});
            skPoint(sketch, "E175.0.2.7", {"position": v(-70, 118.33) * mm});
            skPoint(sketch, "E175.0.2.8", {"position": v(-75, 117.33) * mm});
            skLineSegment(sketch, "E175.0.3.0", {"start": v(-68.25, 32) * mm, "end": v(-71.75, 32) * mm});
            skLineSegment(sketch, "E175.0.3.1", {"start": v(-68.25, 41) * mm, "end": v(-71.75, 41) * mm});
            skLineSegment(sketch, "E175.0.3.2", {"start": v(-68.25, 32) * mm, "end": v(-68.25, 41) * mm});
            skLineSegment(sketch, "E175.0.3.3", {"start": v(-71.75, 32) * mm, "end": v(-71.75, 41) * mm});
            skPoint(sketch, "E175.0.3.4", {"position": v(-70, 37.5) * mm});
            skPoint(sketch, "E175.0.3.5", {"position": v(-75, 36.5) * mm});
            skPoint(sketch, "E175.0.3.6", {"position": v(-70, 36.5) * mm});
            skPoint(sketch, "E175.0.3.7", {"position": v(-70, 37.5) * mm});
            skPoint(sketch, "E175.0.3.8", {"position": v(-75, 36.5) * mm});
            skLineSegment(sketch, "E175.1.0.0", {"start": v(72.55, 274.5) * mm, "end": v(69.05, 274.5) * mm});
            skLineSegment(sketch, "E175.1.0.1", {"start": v(72.55, 283.5) * mm, "end": v(69.05, 283.5) * mm});
            skLineSegment(sketch, "E175.1.0.2", {"start": v(72.55, 274.5) * mm, "end": v(72.55, 283.5) * mm});
            skLineSegment(sketch, "E175.1.0.3", {"start": v(69.05, 274.5) * mm, "end": v(69.05, 283.5) * mm});
            skPoint(sketch, "E175.1.0.4", {"position": v(70.8, 280) * mm});
            skPoint(sketch, "E175.1.0.5", {"position": v(65.8, 279) * mm});
            skPoint(sketch, "E175.1.0.6", {"position": v(70.8, 279) * mm});
            skPoint(sketch, "E175.1.0.7", {"position": v(70.8, 280) * mm});
            skPoint(sketch, "E175.1.0.8", {"position": v(65.8, 279) * mm});
            skLineSegment(sketch, "E175.1.1.0", {"start": v(72.55, 193.67) * mm, "end": v(69.05, 193.67) * mm});
            skLineSegment(sketch, "E175.1.1.1", {"start": v(72.55, 202.67) * mm, "end": v(69.05, 202.67) * mm});
            skLineSegment(sketch, "E175.1.1.2", {"start": v(72.55, 193.67) * mm, "end": v(72.55, 202.67) * mm});
            skLineSegment(sketch, "E175.1.1.3", {"start": v(69.05, 193.67) * mm, "end": v(69.05, 202.67) * mm});
            skPoint(sketch, "E175.1.1.4", {"position": v(70.8, 199.17) * mm});
            skPoint(sketch, "E175.1.1.5", {"position": v(65.8, 198.17) * mm});
            skPoint(sketch, "E175.1.1.6", {"position": v(70.8, 198.17) * mm});
            skPoint(sketch, "E175.1.1.7", {"position": v(70.8, 199.17) * mm});
            skPoint(sketch, "E175.1.1.8", {"position": v(65.8, 198.17) * mm});
            skLineSegment(sketch, "E175.1.2.0", {"start": v(72.55, 112.83) * mm, "end": v(69.05, 112.83) * mm});
            skLineSegment(sketch, "E175.1.2.1", {"start": v(72.55, 121.83) * mm, "end": v(69.05, 121.83) * mm});
            skLineSegment(sketch, "E175.1.2.2", {"start": v(72.55, 112.83) * mm, "end": v(72.55, 121.83) * mm});
            skLineSegment(sketch, "E175.1.2.3", {"start": v(69.05, 112.83) * mm, "end": v(69.05, 121.83) * mm});
            skPoint(sketch, "E175.1.2.4", {"position": v(70.8, 118.33) * mm});
            skPoint(sketch, "E175.1.2.5", {"position": v(65.8, 117.33) * mm});
            skPoint(sketch, "E175.1.2.6", {"position": v(70.8, 117.33) * mm});
            skPoint(sketch, "E175.1.2.7", {"position": v(70.8, 118.33) * mm});
            skPoint(sketch, "E175.1.2.8", {"position": v(65.8, 117.33) * mm});
            skLineSegment(sketch, "E175.1.3.0", {"start": v(72.55, 32) * mm, "end": v(69.05, 32) * mm});
            skLineSegment(sketch, "E175.1.3.1", {"start": v(72.55, 41) * mm, "end": v(69.05, 41) * mm});
            skLineSegment(sketch, "E175.1.3.2", {"start": v(72.55, 32) * mm, "end": v(72.55, 41) * mm});
            skLineSegment(sketch, "E175.1.3.3", {"start": v(69.05, 32) * mm, "end": v(69.05, 41) * mm});
            skPoint(sketch, "E175.1.3.4", {"position": v(70.8, 37.5) * mm});
            skPoint(sketch, "E175.1.3.5", {"position": v(65.8, 36.5) * mm});
            skPoint(sketch, "E175.1.3.6", {"position": v(70.8, 36.5) * mm});
            skPoint(sketch, "E175.1.3.7", {"position": v(70.8, 37.5) * mm});
            skPoint(sketch, "E175.1.3.8", {"position": v(65.8, 36.5) * mm});
            skLineSegment(sketch, "E175.direction1", {"start": v(-71.75, 274.5) * mm, "end": v(69.05, 274.5) * mm, "construction": true});
            skLineSegment(sketch, "E175.direction2", {"start": v(-71.75, 274.5) * mm, "end": v(-71.75, 193.67) * mm, "construction": true});
            skLineSegment(sketch, "E176.bottom", {"start": v(4.5, 278.04) * mm, "end": v(-4.5, 278.04) * mm});
            skLineSegment(sketch, "E176.top", {"start": v(4.5, 281.54) * mm, "end": v(-4.5, 281.54) * mm});
            skLineSegment(sketch, "E176.left", {"start": v(4.5, 278.04) * mm, "end": v(4.5, 281.54) * mm});
            skLineSegment(sketch, "E176.right", {"start": v(-4.5, 278.04) * mm, "end": v(-4.5, 281.54) * mm});
            skPoint(sketch, "E176.middle", {"position": v(0, 279.79) * mm});
            skSolve(sketch);
        }
        {
            var Q0;
            Q0 = qSketchRegion(id + "F15", true);
            extrude(context, id + "F16", {"entities" : qUnion([Q0]), "operationType" : NewBodyOperationType.REMOVE, "oppositeDirection" : true, "depth" : 11.25 * mm});
        }
    });
